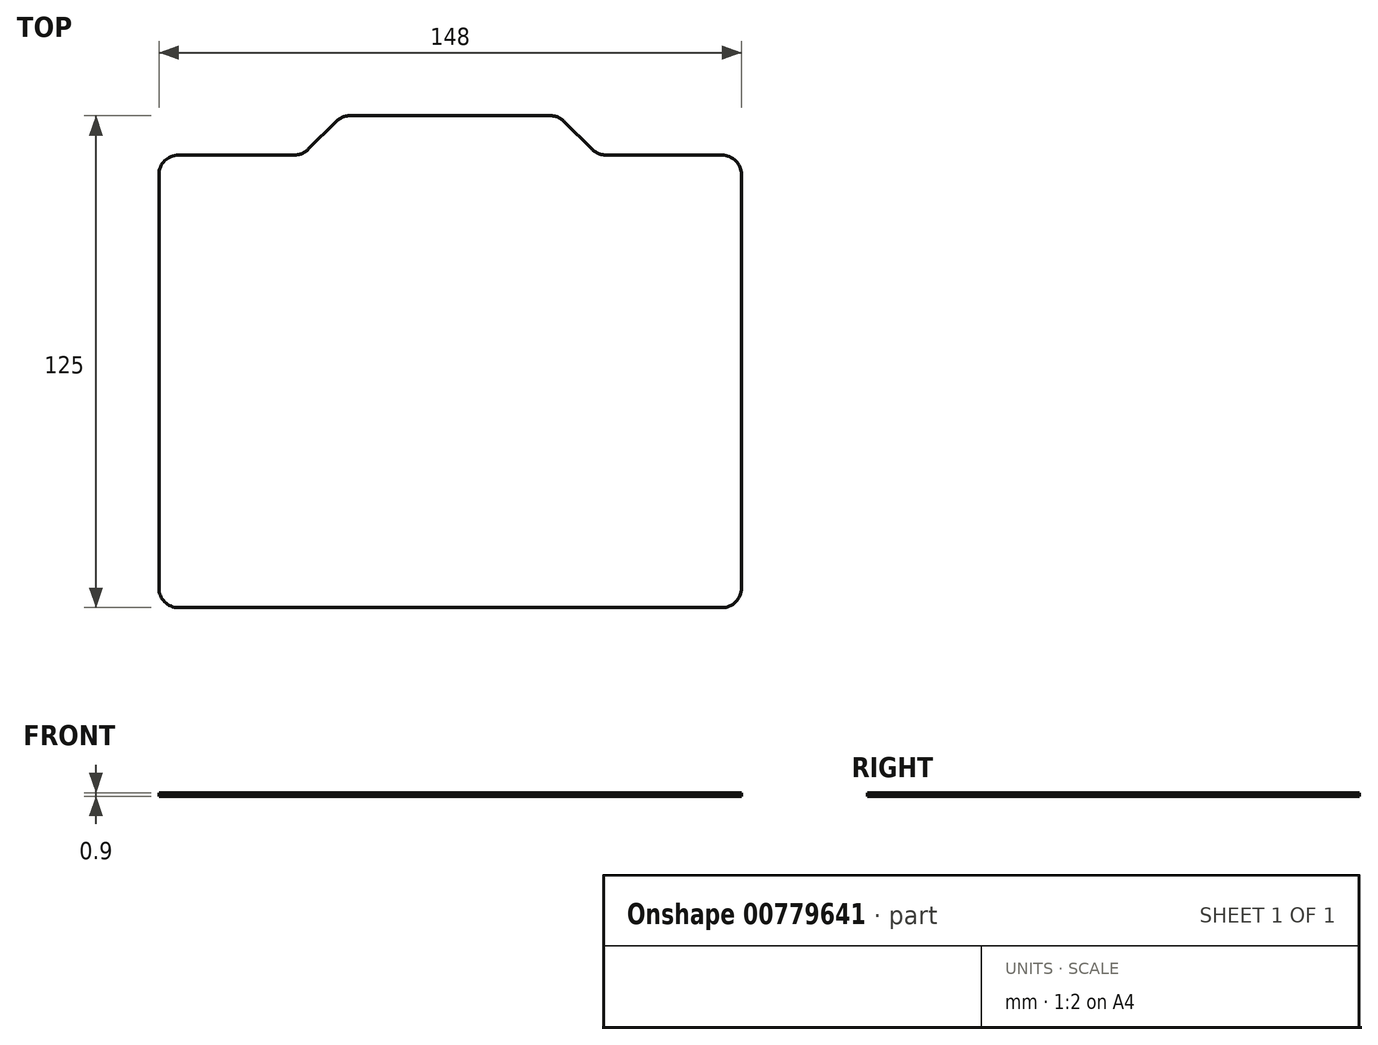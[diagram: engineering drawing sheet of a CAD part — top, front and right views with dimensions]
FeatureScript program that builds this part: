
annotation { "Feature Type Name" : "Feature", "Feature Type Description" : "" }
export const myFeature = defineFeature(function(context is Context, id is Id, definition is map)
    precondition{}
    {
        {
            var Q0;
            Q0=qCreatedBy(makeId("Top.planeOp"),FACE);
            var sketch = newSketch(context, id + "F0", { "sketchPlane" : qUnion([Q0])});
            skLineSegment(sketch, "E0.bottom", {"start": v(74, -59.55) * mm, "end": v(-74, -59.55) * mm});
            skLineSegment(sketch, "E0.left", {"start": v(74, -59.55) * mm, "end": v(74, 55.45) * mm});
            skLineSegment(sketch, "E0.right", {"start": v(-74, -59.55) * mm, "end": v(-74, 55.45) * mm});
            skPoint(sketch, "E0.middle", {"position": v(0, 0) * mm});
            skLineSegment(sketch, "E1", {"start": v(-37.5, 55.45) * mm, "end": v(-74, 55.45) * mm});
            skLineSegment(sketch, "E2", {"start": v(-37.5, 55.45) * mm, "end": v(-27.5, 65.45) * mm});
            skLineSegment(sketch, "E3.MirrorCS", {"start": v(37.5, 55.45) * mm, "end": v(27.5, 65.45) * mm});
            skLineSegment(sketch, "E4", {"start": v(-27.5, 65.45) * mm, "end": v(27.5, 65.45) * mm});
            skLineSegment(sketch, "E5", {"start": v(37.5, 55.45) * mm, "end": v(74, 55.45) * mm});
            skSolve(sketch);
        }
        {
            var Q0;
            Q0=qSketchRegion(id+"F0",true);
            extrude(context, id + "F1", {"entities" : qUnion([Q0]), "depth" : 0.9 * mm});
        }
        {
            var Q0;
            Q0=makeQuery(id+"F1.opExtrude","SWEPT_EDGE",EDGE,{"disambiguationData":[OSD([sQuery(id+"F0.wireOp",EDGE,"E0.left"),sQuery(id+"F0.wireOp",EDGE,"ejG3RJKU-8TXi-9DbA-Vjr5-DWuT4zVf209p")])]});
            var Q1;
            Q1=makeQuery(id+"F1.opExtrude","SWEPT_EDGE",EDGE,{"disambiguationData":[OSD([sQuery(id+"F0.wireOp",EDGE,"E0.top"),sQuery(id+"F0.wireOp",EDGE,"abcLDjcQ-IZLM-86TW-wJfd-IzdS1YfgYfKc")])]});
            var Q2;
            Q2=makeQuery(id+"F1.opExtrude","SWEPT_EDGE",EDGE,{"disambiguationData":[OSD([sQuery(id+"F0.wireOp",EDGE,"E0.top"),sQuery(id+"F0.wireOp",EDGE,"E0.right")])]});
            var Q3;
            Q3=makeQuery(id+"F1.opExtrude","SWEPT_EDGE",EDGE,{"disambiguationData":[OSD([sQuery(id+"F0.wireOp",EDGE,"abcLDjcQ-IZLM-86TW-wJfd-IzdS1YfgYfKc"),sQuery(id+"F0.wireOp",EDGE,"ejG3RJKU-8TXi-9DbA-Vjr5-DWuT4zVf209p")])]});
            var Q4;
            Q4=makeQuery(id+"F1.opExtrude","SWEPT_EDGE",EDGE,{"disambiguationData":[OSD([sQuery(id+"F0.wireOp",EDGE,"E3.MirrorCS"),sQuery(id+"F0.wireOp",EDGE,"E5")])]});
            var Q5;
            Q5=makeQuery(id+"F1.opExtrude","SWEPT_EDGE",EDGE,{"disambiguationData":[OSD([sQuery(id+"F0.wireOp",EDGE,"E3.MirrorCS"),sQuery(id+"F0.wireOp",EDGE,"E4")])]});
            var Q6;
            Q6=makeQuery(id+"F1.opExtrude","SWEPT_EDGE",EDGE,{"disambiguationData":[OSD([sQuery(id+"F0.wireOp",EDGE,"E1"),sQuery(id+"F0.wireOp",EDGE,"E2")])]});
            var Q7;
            Q7=makeQuery(id+"F1.opExtrude","SWEPT_EDGE",EDGE,{"disambiguationData":[OSD([sQuery(id+"F0.wireOp",EDGE,"E2"),sQuery(id+"F0.wireOp",EDGE,"E4")])]});
            fillet(context, id + "F2", {"entities" : qUnion([Q0, Q1, Q2, Q3, Q4, Q5, Q6, Q7]), "radius" : 5 * mm, "tangentPropagation" : true, "allowEdgeOverflow" : false});
        }
    });
